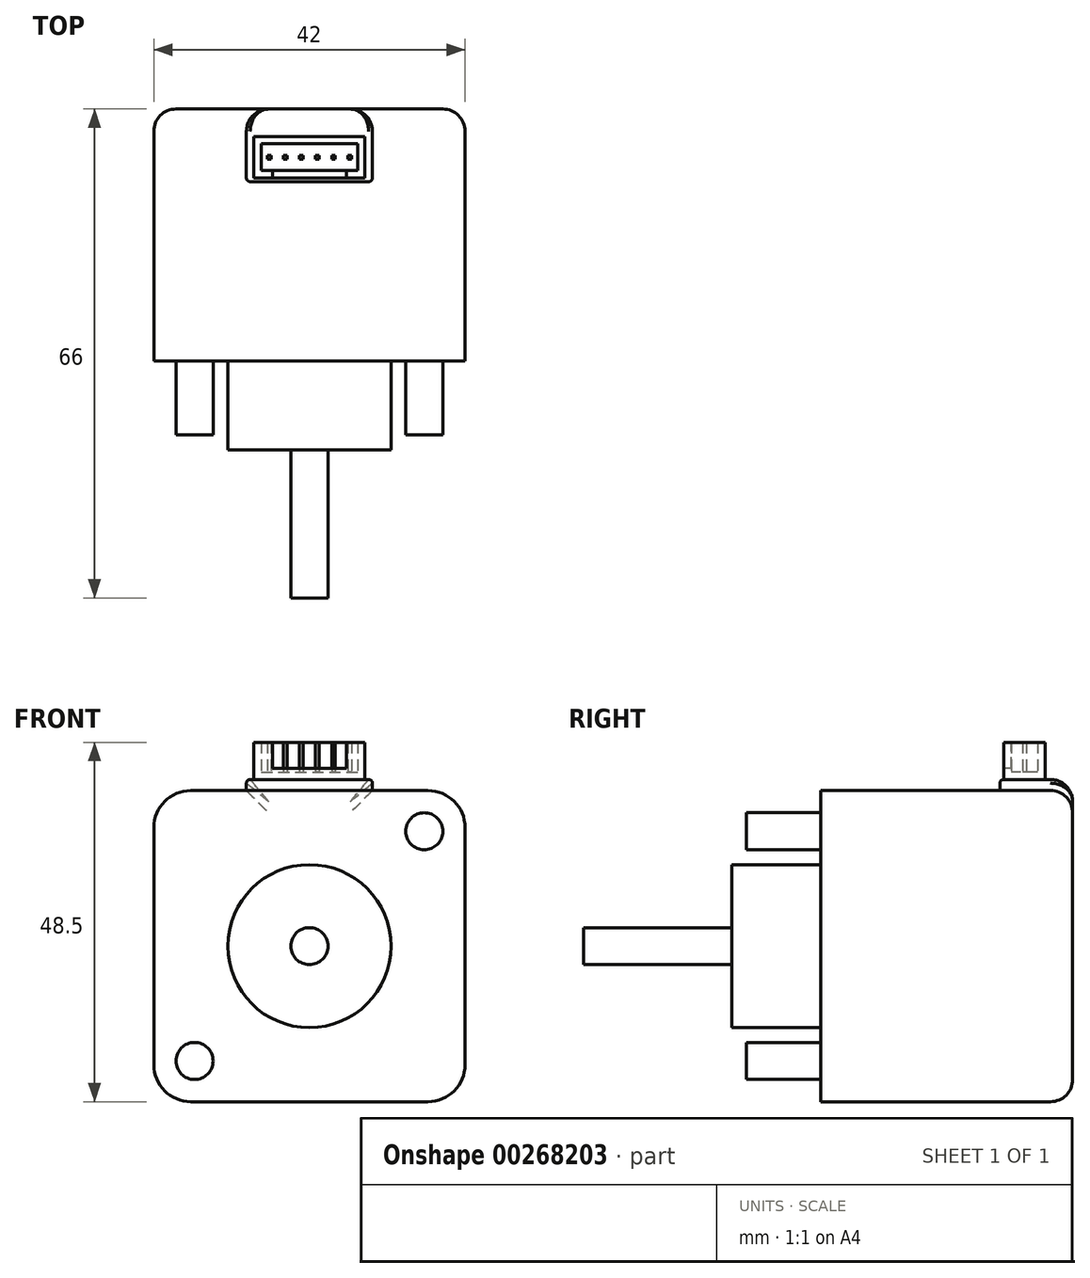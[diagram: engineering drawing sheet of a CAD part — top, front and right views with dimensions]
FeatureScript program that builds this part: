
annotation { "Feature Type Name" : "Feature", "Feature Type Description" : "" }
export const myFeature = defineFeature(function(context is Context, id is Id, definition is map)
    precondition{}
    {
        {
            var Q0;
            Q0=qCreatedBy(makeId("Front.planeOp"),FACE);
            var sketch = newSketch(context, id + "F0", { "sketchPlane" : qUnion([Q0])});
            skLineSegment(sketch, "E0.bottom", {"start": v(-21, 21) * mm, "end": v(21, 21) * mm});
            skLineSegment(sketch, "E0.top", {"start": v(-21, -21) * mm, "end": v(21, -21) * mm});
            skLineSegment(sketch, "E0.left", {"start": v(-21, 21) * mm, "end": v(-21, -21) * mm});
            skLineSegment(sketch, "E0.right", {"start": v(21, 21) * mm, "end": v(21, -21) * mm});
            skSolve(sketch);
        }
        {
            var Q0;
            Q0=makeQuery(id+"F0.imprint","IMPRINT",FACE,{"disambiguationData":[TD([[makeQuery(id+"F0.imprint","IMPRINT",EDGE,{"derivedFrom":sQuery(id+"F0.wireOp",EDGE,"E0.bottom")}),-1.0]])]});
            extrude(context, id + "F1", {"entities" : qUnion([Q0]), "depth" : 44 * mm});
        }
        {
            var Q0;
            Q0=makeQuery(id+"F1.opExtrude","CAP_FACE",FACE,{"disambiguationData":[OSD([sQuery(id+"F0.wireOp",EDGE,"E0.bottom"),sQuery(id+"F0.wireOp",EDGE,"E0.top"),sQuery(id+"F0.wireOp",EDGE,"E0.left"),sQuery(id+"F0.wireOp",EDGE,"E0.right")])],"isStart":false});
            var sketch = newSketch(context, id + "F2", { "sketchPlane" : qUnion([Q0])});
            skCircle(sketch, "E1", {"center": v(0, 0) * mm, "radius": 11 * mm});
            skSolve(sketch);
        }
        {
            var Q0;
            Q0=makeQuery(id+"F2.imprint","IMPRINT",FACE,{"disambiguationData":[TD([[makeQuery(id+"F2.imprint","IMPRINT",EDGE,{"derivedFrom":sQuery(id+"F2.wireOp",EDGE,"E1")}),1.0]])]});
            extrude(context, id + "F3", {"entities" : qUnion([Q0]), "operationType" : NewBodyOperationType.ADD, "depth" : 2 * mm});
        }
        {
            var Q0;
            Q0=makeQuery(id+"F3.opExtrude","CAP_FACE",FACE,{"disambiguationData":[OSD([sQuery(id+"F2.wireOp",EDGE,"E1")])],"isStart":false});
            var sketch = newSketch(context, id + "F4", { "sketchPlane" : qUnion([Q0])});
            skCircle(sketch, "E2", {"center": v(0, 0) * mm, "radius": 2.5 * mm});
            skSolve(sketch);
        }
        {
            var Q0;
            Q0=makeQuery(id+"F4.imprint","IMPRINT",FACE,{"disambiguationData":[TD([[makeQuery(id+"F4.imprint","IMPRINT",EDGE,{"derivedFrom":sQuery(id+"F4.wireOp",EDGE,"E2")}),1.0]])]});
            extrude(context, id + "F5", {"entities" : qUnion([Q0]), "operationType" : NewBodyOperationType.ADD, "depth" : 20 * mm});
        }
        {
            var Q0;
            Q0=makeQuery(id+"F1.opExtrude","CAP_FACE",FACE,{"disambiguationData":[OSD([sQuery(id+"F0.wireOp",EDGE,"E0.bottom"),sQuery(id+"F0.wireOp",EDGE,"E0.top"),sQuery(id+"F0.wireOp",EDGE,"E0.left"),sQuery(id+"F0.wireOp",EDGE,"E0.right")])],"isStart":false});
            var sketch = newSketch(context, id + "F6", { "sketchPlane" : qUnion([Q0])});
            skCircle(sketch, "E3", {"center": v(-15.5, 15.5) * mm, "radius": 2.5 * mm});
            skCircle(sketch, "E4.MirrorC", {"center": v(15.5, 15.5) * mm, "radius": 2.5 * mm});
            skCircle(sketch, "E5.MirrorC", {"center": v(-15.5, -15.5) * mm, "radius": 2.5 * mm});
            skCircle(sketch, "E6.MirrorC", {"center": v(15.5, -15.5) * mm, "radius": 2.5 * mm});
            skSolve(sketch);
        }
        {
            var Q0;
            Q0=makeQuery(id+"F6.imprint","IMPRINT",FACE,{"disambiguationData":[TD([[makeQuery(id+"F6.imprint","IMPRINT",EDGE,{"derivedFrom":sQuery(id+"F6.wireOp",EDGE,"E3")}),1.0]])]});
            var Q1;
            Q1=makeQuery(id+"F6.imprint","IMPRINT",FACE,{"disambiguationData":[TD([[makeQuery(id+"F6.imprint","IMPRINT",EDGE,{"derivedFrom":sQuery(id+"F6.wireOp",EDGE,"E4.MirrorC")}),-1.0]])]});
            var Q2;
            Q2=makeQuery(id+"F6.imprint","IMPRINT",FACE,{"disambiguationData":[TD([[makeQuery(id+"F6.imprint","IMPRINT",EDGE,{"derivedFrom":sQuery(id+"F6.wireOp",EDGE,"E6.MirrorC")}),1.0]])]});
            var Q3;
            Q3=makeQuery(id+"F6.imprint","IMPRINT",FACE,{"disambiguationData":[TD([[makeQuery(id+"F6.imprint","IMPRINT",EDGE,{"derivedFrom":sQuery(id+"F6.wireOp",EDGE,"E5.MirrorC")}),-1.0]])]});
            extrude(context, id + "F7", {"entities" : qUnion([Q0, Q1, Q2, Q3]), "operationType" : NewBodyOperationType.REMOVE, "oppositeDirection" : true, "depth" : 10 * mm});
        }
        {
            var Q0;
            Q0=makeQuery(id+"F1.opExtrude","SWEPT_FACE",FACE,{"disambiguationData":[OSD([sQuery(id+"F0.wireOp",EDGE,"E0.bottom")])]});
            var sketch = newSketch(context, id + "F8", { "sketchPlane" : qUnion([Q0])});
            skLineSegment(sketch, "E7.bottom", {"start": v(-8.5, 0) * mm, "end": v(8.5, 0) * mm});
            skLineSegment(sketch, "E7.top", {"start": v(-8.5, -9.8) * mm, "end": v(8.5, -9.8) * mm});
            skLineSegment(sketch, "E7.left", {"start": v(-8.5, 0) * mm, "end": v(-8.5, -9.8) * mm});
            skLineSegment(sketch, "E7.right", {"start": v(8.5, 0) * mm, "end": v(8.5, -9.8) * mm});
            skSolve(sketch);
        }
        {
            var Q0;
            Q0=makeQuery(id+"F8.imprint","IMPRINT",FACE,{"disambiguationData":[TD([[makeQuery(id+"F8.imprint","IMPRINT",EDGE,{"derivedFrom":sQuery(id+"F8.wireOp",EDGE,"E7.bottom")}),-1.0]])]});
            extrude(context, id + "F9", {"entities" : qUnion([Q0]), "operationType" : NewBodyOperationType.ADD, "depth" : 1.5 * mm});
        }
        {
            var Q0;
            Q0=makeQuery(id+"F1.opExtrude","SWEPT_EDGE",EDGE,{"disambiguationData":[OSD([sQuery(id+"F0.wireOp",EDGE,"E0.bottom"),sQuery(id+"F0.wireOp",EDGE,"E0.left")])]});
            var Q1;
            Q1=makeQuery(id+"F1.opExtrude","SWEPT_EDGE",EDGE,{"disambiguationData":[OSD([sQuery(id+"F0.wireOp",EDGE,"E0.bottom"),sQuery(id+"F0.wireOp",EDGE,"E0.right")])]});
            var Q2;
            Q2=makeQuery(id+"F1.opExtrude","SWEPT_EDGE",EDGE,{"disambiguationData":[OSD([sQuery(id+"F0.wireOp",EDGE,"E0.top"),sQuery(id+"F0.wireOp",EDGE,"E0.right")])]});
            var Q3;
            Q3=makeQuery(id+"F1.opExtrude","SWEPT_EDGE",EDGE,{"disambiguationData":[OSD([sQuery(id+"F0.wireOp",EDGE,"E0.top"),sQuery(id+"F0.wireOp",EDGE,"E0.left")])]});
            fillet(context, id + "F10", {"entities" : qUnion([Q0, Q1, Q2, Q3]), "radius" : 5 * mm, "tangentPropagation" : true, "allowEdgeOverflow" : false});
        }
        {
            var Q0;
            Q0=makeQuery(id+"F9.boolean.opBoolean","MERGE",FACE,{"derivedFrom":[makeQuery(id+"F1.opExtrude","CAP_FACE",FACE,{"disambiguationData":[OSD([sQuery(id+"F0.wireOp",EDGE,"E0.bottom"),sQuery(id+"F0.wireOp",EDGE,"E0.top"),sQuery(id+"F0.wireOp",EDGE,"E0.left"),sQuery(id+"F0.wireOp",EDGE,"E0.right")])],"isStart":true}),makeQuery(id+"F9.opExtrude","SWEPT_FACE",FACE,{"disambiguationData":[OSD([sQuery(id+"F8.wireOp",EDGE,"E7.bottom")])]})]});
            fillet(context, id + "F11", {"entities" : qUnion([Q0]), "radius" : 3 * mm, "tangentPropagation" : true, "allowEdgeOverflow" : false});
        }
        {
            var Q0;
            Q0=makeQuery(id+"F9.opExtrude","CAP_FACE",FACE,{"disambiguationData":[OSD([sQuery(id+"F8.wireOp",EDGE,"E7.bottom"),sQuery(id+"F8.wireOp",EDGE,"E7.top"),sQuery(id+"F8.wireOp",EDGE,"E7.left"),sQuery(id+"F8.wireOp",EDGE,"E7.right")])],"isStart":false});
            var sketch = newSketch(context, id + "F12", { "sketchPlane" : qUnion([Q0])});
            skLineSegment(sketch, "E8.bottom", {"start": v(-7.5, -3.7) * mm, "end": v(7.5, -3.7) * mm});
            skLineSegment(sketch, "E8.top", {"start": v(-7.5, -9.3) * mm, "end": v(7.5, -9.3) * mm});
            skLineSegment(sketch, "E8.left", {"start": v(-7.5, -3.7) * mm, "end": v(-7.5, -9.3) * mm});
            skLineSegment(sketch, "E8.right", {"start": v(7.5, -3.7) * mm, "end": v(7.5, -9.3) * mm});
            skSolve(sketch);
        }
        {
            var Q0;
            Q0=makeQuery(id+"F12.imprint","IMPRINT",FACE,{"disambiguationData":[TD([[makeQuery(id+"F12.imprint","IMPRINT",EDGE,{"derivedFrom":sQuery(id+"F12.wireOp",EDGE,"E8.bottom")}),-1.0]])]});
            extrude(context, id + "F13", {"entities" : qUnion([Q0]), "operationType" : NewBodyOperationType.ADD, "depth" : 1 * mm});
        }
        {
            var Q0;
            Q0=makeQuery(id+"F13.opExtrude","CAP_FACE",FACE,{"disambiguationData":[OSD([sQuery(id+"F12.wireOp",EDGE,"E8.bottom"),sQuery(id+"F12.wireOp",EDGE,"E8.top"),sQuery(id+"F12.wireOp",EDGE,"E8.left"),sQuery(id+"F12.wireOp",EDGE,"E8.right")])],"isStart":false});
            var sketch = newSketch(context, id + "F14", { "sketchPlane" : qUnion([Q0])});
            skLineSegment(sketch, "E9.bottom", {"start": v(-6.5, -4.7) * mm, "end": v(6.5, -4.7) * mm});
            skLineSegment(sketch, "E9.top", {"start": v(-6.5, -8.3) * mm, "end": v(6.5, -8.3) * mm});
            skLineSegment(sketch, "E9.left", {"start": v(-6.5, -4.7) * mm, "end": v(-6.5, -8.3) * mm});
            skLineSegment(sketch, "E9.right", {"start": v(6.5, -4.7) * mm, "end": v(6.5, -8.3) * mm});
            skSolve(sketch);
        }
        {
            var Q0;
            Q0=makeQuery(id+"F14.imprint","IMPRINT",FACE,{"disambiguationData":[TD([[makeQuery(id+"F14.imprint","IMPRINT",EDGE,{"derivedFrom":sQuery(id+"F14.wireOp",EDGE,"E9.bottom")}),1.0]])]});
            extrude(context, id + "F15", {"entities" : qUnion([Q0]), "operationType" : NewBodyOperationType.ADD, "depth" : 4 * mm});
        }
        {
            var Q0;
            Q0=makeQuery(id+"F13.opExtrude","CAP_FACE",FACE,{"disambiguationData":[OSD([sQuery(id+"F12.wireOp",EDGE,"E8.bottom"),sQuery(id+"F12.wireOp",EDGE,"E8.top"),sQuery(id+"F12.wireOp",EDGE,"E8.left"),sQuery(id+"F12.wireOp",EDGE,"E8.right")])],"isStart":false});
            var sketch = newSketch(context, id + "F16", { "sketchPlane" : qUnion([Q0])});
            skLineSegment(sketch, "E10.bottom", {"start": v(-5.67, -6.25) * mm, "end": v(-5.17, -6.25) * mm});
            skLineSegment(sketch, "E10.top", {"start": v(-5.67, -6.75) * mm, "end": v(-5.17, -6.75) * mm});
            skLineSegment(sketch, "E10.left", {"start": v(-5.67, -6.25) * mm, "end": v(-5.67, -6.75) * mm});
            skLineSegment(sketch, "E10.right", {"start": v(-5.17, -6.25) * mm, "end": v(-5.17, -6.75) * mm});
            skLineSegment(sketch, "E11.bottom", {"start": v(-3.5, -6.25) * mm, "end": v(-3, -6.25) * mm});
            skLineSegment(sketch, "E11.top", {"start": v(-3.5, -6.75) * mm, "end": v(-3, -6.75) * mm});
            skLineSegment(sketch, "E11.left", {"start": v(-3.5, -6.25) * mm, "end": v(-3.5, -6.75) * mm});
            skLineSegment(sketch, "E11.right", {"start": v(-3, -6.25) * mm, "end": v(-3, -6.75) * mm});
            skLineSegment(sketch, "E12.bottom", {"start": v(-1.33, -6.25) * mm, "end": v(-0.83, -6.25) * mm});
            skLineSegment(sketch, "E12.top", {"start": v(-1.33, -6.75) * mm, "end": v(-0.83, -6.75) * mm});
            skLineSegment(sketch, "E12.left", {"start": v(-1.33, -6.25) * mm, "end": v(-1.33, -6.75) * mm});
            skLineSegment(sketch, "E12.right", {"start": v(-0.83, -6.25) * mm, "end": v(-0.83, -6.75) * mm});
            skLineSegment(sketch, "E13.MirrorCS", {"start": v(3.5, -6.25) * mm, "end": v(3, -6.25) * mm});
            skLineSegment(sketch, "E14.MirrorCS", {"start": v(3.5, -6.25) * mm, "end": v(3.5, -6.75) * mm});
            skLineSegment(sketch, "E15.MirrorCS", {"start": v(3, -6.25) * mm, "end": v(3, -6.75) * mm});
            skLineSegment(sketch, "E16.MirrorCS", {"start": v(3.5, -6.75) * mm, "end": v(3, -6.75) * mm});
            skLineSegment(sketch, "E17.MirrorCS", {"start": v(1.33, -6.25) * mm, "end": v(1.33, -6.75) * mm});
            skLineSegment(sketch, "E18.MirrorCS", {"start": v(1.33, -6.25) * mm, "end": v(0.83, -6.25) * mm});
            skLineSegment(sketch, "E19.MirrorCS", {"start": v(0.83, -6.25) * mm, "end": v(0.83, -6.75) * mm});
            skLineSegment(sketch, "E20.MirrorCS", {"start": v(1.33, -6.75) * mm, "end": v(0.83, -6.75) * mm});
            skLineSegment(sketch, "E21.MirrorCS", {"start": v(5.67, -6.75) * mm, "end": v(5.17, -6.75) * mm});
            skLineSegment(sketch, "E22.MirrorCS", {"start": v(5.17, -6.25) * mm, "end": v(5.17, -6.75) * mm});
            skLineSegment(sketch, "E23.MirrorCS", {"start": v(5.67, -6.25) * mm, "end": v(5.17, -6.25) * mm});
            skLineSegment(sketch, "E24.MirrorCS", {"start": v(5.67, -6.25) * mm, "end": v(5.67, -6.75) * mm});
            skSolve(sketch);
        }
        {
            var Q0;
            Q0=makeQuery(id+"F16.imprint","IMPRINT",FACE,{"disambiguationData":[TD([[makeQuery(id+"F16.imprint","IMPRINT",EDGE,{"derivedFrom":sQuery(id+"F16.wireOp",EDGE,"E10.bottom")}),-1.0]])]});
            var Q1;
            Q1=makeQuery(id+"F16.imprint","IMPRINT",FACE,{"disambiguationData":[TD([[makeQuery(id+"F16.imprint","IMPRINT",EDGE,{"derivedFrom":sQuery(id+"F16.wireOp",EDGE,"E11.bottom")}),-1.0]])]});
            var Q2;
            Q2=makeQuery(id+"F16.imprint","IMPRINT",FACE,{"disambiguationData":[TD([[makeQuery(id+"F16.imprint","IMPRINT",EDGE,{"derivedFrom":sQuery(id+"F16.wireOp",EDGE,"E12.bottom")}),-1.0]])]});
            var Q3;
            Q3=makeQuery(id+"F16.imprint","IMPRINT",FACE,{"disambiguationData":[TD([[makeQuery(id+"F16.imprint","IMPRINT",EDGE,{"derivedFrom":sQuery(id+"F16.wireOp",EDGE,"E13.MirrorCS")}),1.0]])]});
            var Q4;
            Q4=makeQuery(id+"F16.imprint","IMPRINT",FACE,{"disambiguationData":[TD([[makeQuery(id+"F16.imprint","IMPRINT",EDGE,{"derivedFrom":sQuery(id+"F16.wireOp",EDGE,"E17.MirrorCS")}),-1.0]])]});
            var Q5;
            Q5=makeQuery(id+"F16.imprint","IMPRINT",FACE,{"disambiguationData":[TD([[makeQuery(id+"F16.imprint","IMPRINT",EDGE,{"derivedFrom":sQuery(id+"F16.wireOp",EDGE,"E21.MirrorCS")}),-1.0]])]});
            extrude(context, id + "F17", {"entities" : qUnion([Q0, Q1, Q2, Q3, Q4, Q5]), "operationType" : NewBodyOperationType.ADD, "depth" : 4 * mm});
        }
        {
            var Q0;
            Q0=makeQuery(id+"F9.opExtrude","CAP_EDGE",EDGE,{"disambiguationData":[OSD([sQuery(id+"F8.wireOp",EDGE,"E7.top")])],"isStart":false});
            var Q1;
            Q1=makeQuery(id+"F9.opExtrude","SWEPT_EDGE",EDGE,{"disambiguationData":[OSD([sQuery(id+"F8.wireOp",EDGE,"E7.top"),sQuery(id+"F8.wireOp",EDGE,"E7.right")])]});
            var Q2;
            Q2=makeQuery(id+"F9.opExtrude","CAP_EDGE",EDGE,{"disambiguationData":[OSD([sQuery(id+"F8.wireOp",EDGE,"E7.right")])],"isStart":false});
            var Q3;
            Q3=makeQuery(id+"F9.opExtrude","SWEPT_EDGE",EDGE,{"disambiguationData":[OSD([sQuery(id+"F8.wireOp",EDGE,"E7.top"),sQuery(id+"F8.wireOp",EDGE,"E7.left")])]});
            var Q4;
            Q4=makeQuery(id+"F9.opExtrude","CAP_EDGE",EDGE,{"disambiguationData":[OSD([sQuery(id+"F8.wireOp",EDGE,"E7.left")])],"isStart":false});
            var Q5;
            {var subQ0=sQuery(id+"F8.wireOp",EDGE,"E7.bottom");Q5=makeQuery(id+"F11.opFillet","BLEND_EDGE",EDGE,{"blendedFrom":[makeQuery(id+"F9.opExtrude","SWEPT_EDGE",EDGE,{"disambiguationData":[OSD([sQuery(id+"F0.wireOp",EDGE,"E0.bottom"),subQ0,sQuery(id+"F8.wireOp",EDGE,"E7.left")])]}),makeQuery(id+"F9.opExtrude","CAP_EDGE",EDGE,{"disambiguationData":[OSD([subQ0])],"isStart":false})],"blendedInto":[]});}
            var Q6;
            {var subQ0=sQuery(id+"F8.wireOp",EDGE,"E7.bottom");Q6=makeQuery(id+"F11.opFillet","BLEND_EDGE",EDGE,{"blendedFrom":[makeQuery(id+"F9.opExtrude","SWEPT_EDGE",EDGE,{"disambiguationData":[OSD([sQuery(id+"F0.wireOp",EDGE,"E0.bottom"),subQ0,sQuery(id+"F8.wireOp",EDGE,"E7.right")])]}),makeQuery(id+"F9.opExtrude","CAP_EDGE",EDGE,{"disambiguationData":[OSD([subQ0])],"isStart":false})],"blendedInto":[]});}
            var Q7;
            {var subQ0=sQuery(id+"F8.wireOp",EDGE,"E7.bottom");Q7=makeQuery(id+"F11.opFillet","BLEND_EDGE",EDGE,{"blendedFrom":[makeQuery(id+"F9.opExtrude","CAP_EDGE",EDGE,{"disambiguationData":[OSD([subQ0])],"isStart":false}),makeQuery(id+"F9.boolean.opBoolean","MERGE",FACE,{"derivedFrom":[makeQuery(id+"F1.opExtrude","CAP_FACE",FACE,{"disambiguationData":[OSD([sQuery(id+"F0.wireOp",EDGE,"E0.bottom"),sQuery(id+"F0.wireOp",EDGE,"E0.top"),sQuery(id+"F0.wireOp",EDGE,"E0.left"),sQuery(id+"F0.wireOp",EDGE,"E0.right")])],"isStart":true}),makeQuery(id+"F9.opExtrude","SWEPT_FACE",FACE,{"disambiguationData":[OSD([subQ0])]})]})],"blendedInto":[makeQuery(id+"F9.boolean.opBoolean","MERGE",FACE,{"derivedFrom":[makeQuery(id+"F1.opExtrude","CAP_FACE",FACE,{"disambiguationData":[OSD([sQuery(id+"F0.wireOp",EDGE,"E0.bottom"),sQuery(id+"F0.wireOp",EDGE,"E0.top"),sQuery(id+"F0.wireOp",EDGE,"E0.left"),sQuery(id+"F0.wireOp",EDGE,"E0.right")])],"isStart":true}),makeQuery(id+"F9.opExtrude","SWEPT_FACE",FACE,{"disambiguationData":[OSD([subQ0])]})]})]});}
            var Q8;
            {var subQ0=sQuery(id+"F8.wireOp",EDGE,"E7.bottom");var subQ1=sQuery(id+"F0.wireOp",EDGE,"E0.bottom");Q8=makeQuery(id+"F11.opFillet","BLEND_EDGE",EDGE,{"blendedFrom":[makeQuery(id+"F9.opExtrude","SWEPT_EDGE",EDGE,{"disambiguationData":[OSD([subQ1,subQ0,sQuery(id+"F8.wireOp",EDGE,"E7.right")])]}),makeQuery(id+"F9.boolean.opBoolean","MERGE",FACE,{"derivedFrom":[makeQuery(id+"F1.opExtrude","CAP_FACE",FACE,{"disambiguationData":[OSD([subQ1,sQuery(id+"F0.wireOp",EDGE,"E0.top"),sQuery(id+"F0.wireOp",EDGE,"E0.left"),sQuery(id+"F0.wireOp",EDGE,"E0.right")])],"isStart":true}),makeQuery(id+"F9.opExtrude","SWEPT_FACE",FACE,{"disambiguationData":[OSD([subQ0])]})]})],"blendedInto":[makeQuery(id+"F9.boolean.opBoolean","MERGE",FACE,{"derivedFrom":[makeQuery(id+"F1.opExtrude","CAP_FACE",FACE,{"disambiguationData":[OSD([subQ1,sQuery(id+"F0.wireOp",EDGE,"E0.top"),sQuery(id+"F0.wireOp",EDGE,"E0.left"),sQuery(id+"F0.wireOp",EDGE,"E0.right")])],"isStart":true}),makeQuery(id+"F9.opExtrude","SWEPT_FACE",FACE,{"disambiguationData":[OSD([subQ0])]})]})]});}
            var Q9;
            {var subQ0=sQuery(id+"F8.wireOp",EDGE,"E7.bottom");var subQ1=sQuery(id+"F0.wireOp",EDGE,"E0.bottom");Q9=makeQuery(id+"F11.opFillet","BLEND_EDGE",EDGE,{"blendedFrom":[makeQuery(id+"F9.opExtrude","SWEPT_EDGE",EDGE,{"disambiguationData":[OSD([subQ1,subQ0,sQuery(id+"F8.wireOp",EDGE,"E7.left")])]}),makeQuery(id+"F9.boolean.opBoolean","MERGE",FACE,{"derivedFrom":[makeQuery(id+"F1.opExtrude","CAP_FACE",FACE,{"disambiguationData":[OSD([subQ1,sQuery(id+"F0.wireOp",EDGE,"E0.top"),sQuery(id+"F0.wireOp",EDGE,"E0.left"),sQuery(id+"F0.wireOp",EDGE,"E0.right")])],"isStart":true}),makeQuery(id+"F9.opExtrude","SWEPT_FACE",FACE,{"disambiguationData":[OSD([subQ0])]})]})],"blendedInto":[makeQuery(id+"F9.boolean.opBoolean","MERGE",FACE,{"derivedFrom":[makeQuery(id+"F1.opExtrude","CAP_FACE",FACE,{"disambiguationData":[OSD([subQ1,sQuery(id+"F0.wireOp",EDGE,"E0.top"),sQuery(id+"F0.wireOp",EDGE,"E0.left"),sQuery(id+"F0.wireOp",EDGE,"E0.right")])],"isStart":true}),makeQuery(id+"F9.opExtrude","SWEPT_FACE",FACE,{"disambiguationData":[OSD([subQ0])]})]})]});}
            fillet(context, id + "F18", {"entities" : qUnion([Q0, Q1, Q2, Q3, Q4, Q5, Q6, Q7, Q8, Q9]), "radius" : .5 * mm, "tangentPropagation" : true, "allowEdgeOverflow" : false});
        }
        {
            var Q0;
            Q0=makeQuery(id+"F15.opExtrude","CAP_FACE",FACE,{"disambiguationData":[OSD([sQuery(id+"F12.wireOp",EDGE,"E8.bottom"),sQuery(id+"F12.wireOp",EDGE,"E8.top"),sQuery(id+"F12.wireOp",EDGE,"E8.left"),sQuery(id+"F12.wireOp",EDGE,"E8.right"),sQuery(id+"F14.wireOp",EDGE,"E9.bottom"),sQuery(id+"F14.wireOp",EDGE,"E9.top"),sQuery(id+"F14.wireOp",EDGE,"E9.left"),sQuery(id+"F14.wireOp",EDGE,"E9.right")])],"isStart":false});
            var sketch = newSketch(context, id + "F19", { "sketchPlane" : qUnion([Q0])});
            skLineSegment(sketch, "E25", {"start": v(-5, -8.3) * mm, "end": v(-5, -9.3) * mm});
            skLineSegment(sketch, "E26", {"start": v(5, -8.3) * mm, "end": v(5, -9.3) * mm});
            skSolve(sketch);
        }
        {
            var Q0;
            {var subQ0=sQuery(id+"F19.wireOp",EDGE,"E25");Q0=makeQuery(id+"F19.imprint","IMPRINT",FACE,{"disambiguationData":[TD([[makeQuery(id+"F19.imprint","IMPRINT",EDGE,{"derivedFrom":subQ0}),1.0]])]});}
            extrude(context, id + "F20", {"entities" : qUnion([Q0]), "operationType" : NewBodyOperationType.REMOVE, "oppositeDirection" : true, "depth" : 3.5 * mm});
        }
    });
